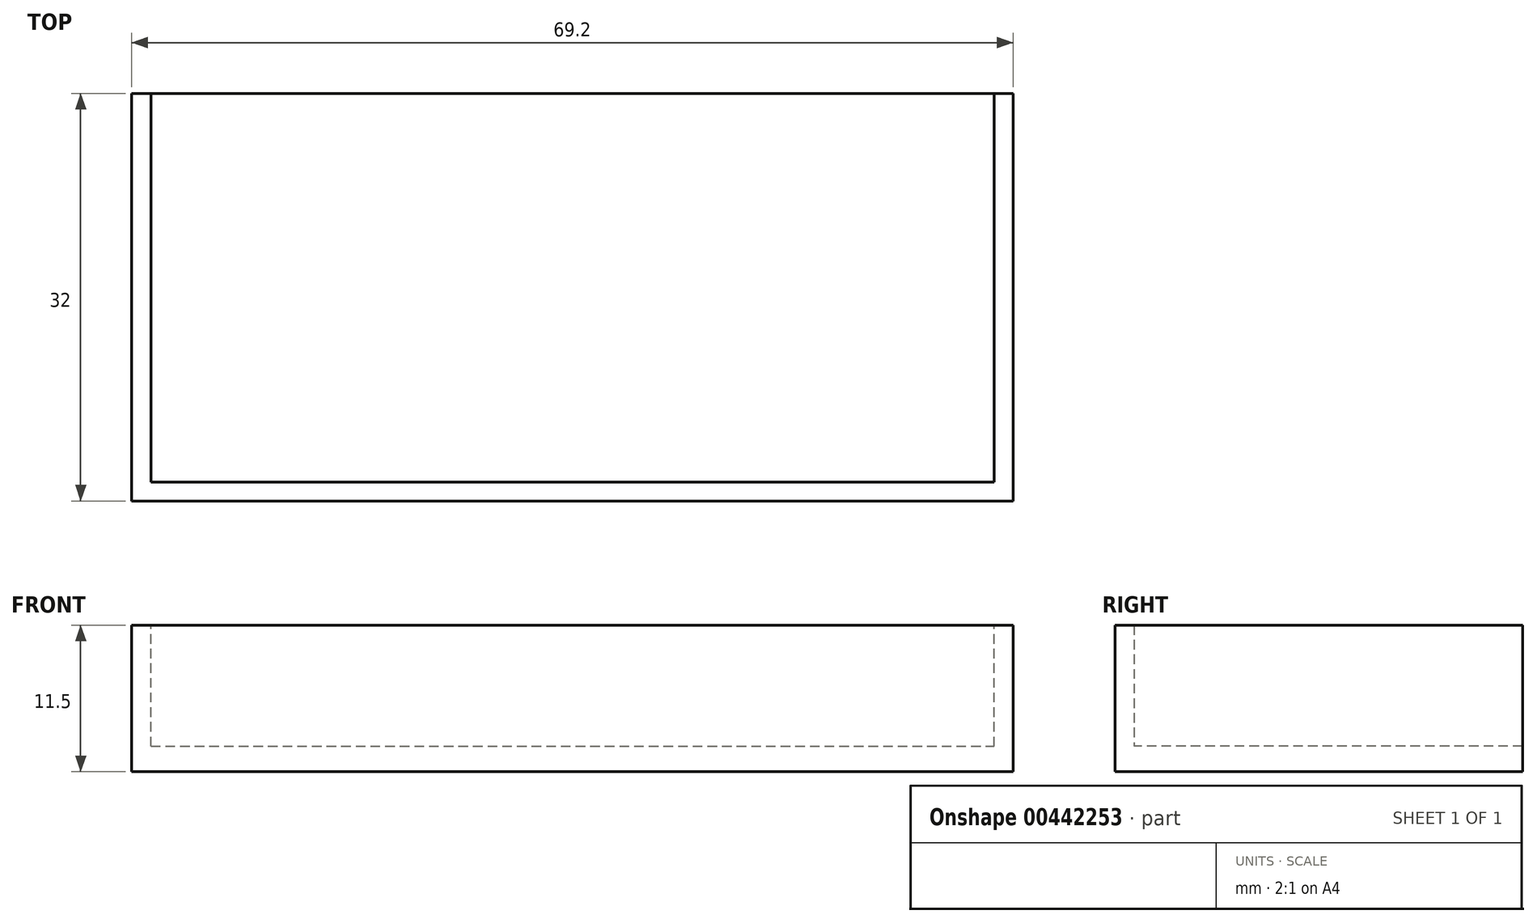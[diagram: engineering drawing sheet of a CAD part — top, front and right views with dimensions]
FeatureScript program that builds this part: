
annotation { "Feature Type Name" : "Feature", "Feature Type Description" : "" }
export const myFeature = defineFeature(function(context is Context, id is Id, definition is map)
    precondition{}
    {
        {
            var Q0;
            Q0=qCreatedBy(makeId("Top.planeOp"),FACE);
            var sketch = newSketch(context, id + "F0", { "sketchPlane" : qUnion([Q0])});
            skLineSegment(sketch, "E0.bottom", {"start": v(0, 0) * mm, "end": v(69.2, 0) * mm});
            skLineSegment(sketch, "E0.top", {"start": v(0, 32) * mm, "end": v(69.2, 32) * mm});
            skLineSegment(sketch, "E0.left", {"start": v(0, 0) * mm, "end": v(0, 32) * mm});
            skLineSegment(sketch, "E0.right", {"start": v(69.2, 0) * mm, "end": v(69.2, 32) * mm});
            skSolve(sketch);
        }
        {
            var Q0;
            Q0 = qSketchRegion(id + "F0", true);
            extrude(context, id + "F1", {"entities" : qUnion([Q0]), "depth" : 2 * mm});
        }
        {
            var Q0;
            Q0=makeQuery(id+"F1.opExtrude","CAP_FACE",FACE,{"disambiguationData":[OSD([sQuery(id+"F0.wireOp",EDGE,"E0.bottom"),sQuery(id+"F0.wireOp",EDGE,"E0.top"),sQuery(id+"F0.wireOp",EDGE,"E0.left"),sQuery(id+"F0.wireOp",EDGE,"E0.right")])],"isStart":false});
            var sketch = newSketch(context, id + "F2", { "sketchPlane" : qUnion([Q0])});
            skLineSegment(sketch, "E1.bottom", {"start": v(0, 32) * mm, "end": v(69.2, 32) * mm});
            skLineSegment(sketch, "E1.top", {"start": v(0, 0) * mm, "end": v(69.2, 0) * mm});
            skLineSegment(sketch, "E1.left", {"start": v(0, 32) * mm, "end": v(0, 0) * mm});
            skLineSegment(sketch, "E1.right", {"start": v(69.2, 32) * mm, "end": v(69.2, 0) * mm});
            skLineSegment(sketch, "E2.bottom", {"start": v(1.5, 30.5) * mm, "end": v(67.7, 30.5) * mm});
            skLineSegment(sketch, "E2.top", {"start": v(1.5, 1.5) * mm, "end": v(67.7, 1.5) * mm});
            skLineSegment(sketch, "E2.left", {"start": v(1.5, 30.5) * mm, "end": v(1.5, 1.5) * mm});
            skLineSegment(sketch, "E2.right", {"start": v(67.7, 30.5) * mm, "end": v(67.7, 1.5) * mm});
            skLineSegment(sketch, "E3", {"start": v(3.5, 30.5) * mm, "end": v(3.5, 32) * mm});
            skLineSegment(sketch, "E4", {"start": v(65.7, 30.5) * mm, "end": v(65.7, 32) * mm});
            skSolve(sketch);
        }
        {
            var Q0;
            Q0=makeQuery(id+"F2.imprint","IMPRINT",FACE,{"disambiguationData":[TD([[makeQuery(id+"F2.imprint","IMPRINT",EDGE,{"derivedFrom":sQuery(id+"F2.wireOp",EDGE,"E1.top")}),1.0]])]});
            extrude(context, id + "F3", {"entities" : qUnion([Q0]), "operationType" : NewBodyOperationType.ADD, "depth" : 9.5 * mm});
        }
        {
            var Q0;
            Q0=makeQuery(id+"F3.opExtrude","CAP_FACE",FACE,{"disambiguationData":[OSD([sQuery(id+"F2.wireOp",EDGE,"E1.bottom"),sQuery(id+"F2.wireOp",EDGE,"E1.top"),sQuery(id+"F2.wireOp",EDGE,"E1.left"),sQuery(id+"F2.wireOp",EDGE,"E1.right"),sQuery(id+"F2.wireOp",EDGE,"E2.bottom"),sQuery(id+"F2.wireOp",EDGE,"E2.top"),sQuery(id+"F2.wireOp",EDGE,"E2.left"),sQuery(id+"F2.wireOp",EDGE,"E2.right"),sQuery(id+"F2.wireOp",EDGE,"E3"),sQuery(id+"F2.wireOp",EDGE,"E4")])],"isStart":false});
            var sketch = newSketch(context, id + "F4", { "sketchPlane" : qUnion([Q0])});
            skLineSegment(sketch, "E5.bottom", {"start": v(1.5, 30.5) * mm, "end": v(67.7, 30.5) * mm});
            skLineSegment(sketch, "E5.top", {"start": v(1.5, 32) * mm, "end": v(67.7, 32) * mm});
            skLineSegment(sketch, "E5.left", {"start": v(1.5, 30.5) * mm, "end": v(1.5, 32) * mm});
            skLineSegment(sketch, "E5.right", {"start": v(67.7, 30.5) * mm, "end": v(67.7, 32) * mm});
            skSolve(sketch);
        }
        {
            var Q0;
            Q0 = qSketchRegion(id + "F4", true);
            extrude(context, id + "F5", {"entities" : qUnion([Q0]), "operationType" : NewBodyOperationType.REMOVE, "oppositeDirection" : true, "depth" : 9.5 * mm});
        }
    });
